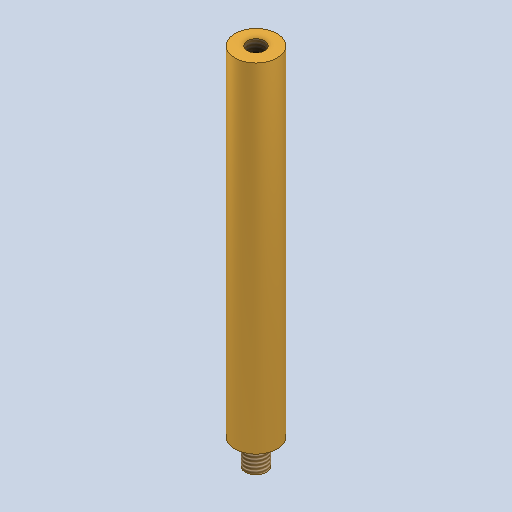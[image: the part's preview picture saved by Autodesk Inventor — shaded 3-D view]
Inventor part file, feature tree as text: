
AUTODESK INVENTOR PART (.ipt)
format: ipt  version: 2023 (Build 270158000, 158)  size: 111,104 bytes
history: native  units: mm
features: sketch x3, extrude x2, other x1, thread x1, hole x1
ambient origin geometry x8: Origin, YZ Plane, XZ Plane, XY Plane, X Axis, Y Axis, Z Axis, Center Point
bodies: Body1 (feature_tree)
feature tree (8):
  other  "Sólido1"
  extrude  "Extrusão1"  Depth=80.0mm TaperAngle=0.0deg
  extrude  "Extrusão3"  Depth=6.0mm TaperAngle=0.0deg
  thread  "Rosca2"  [1 undecoded]
  hole  "Hole1"  [1 undecoded]
  sketch  "Esboço1"  dims[d0=10.0mm d2=80.0mm d3=0.0mm]
  sketch  "Esboço3"  dims[d9=5.0mm d10=6.0mm d11=0.0mm d12=15.0mm d13=0.0mm]
  sketch  "Sketch4"  dims[d14=4.134mm d15=10.0mm d16=4.0mm d17=2.0mm d18=90.0deg d19=14.2mm d20=20.594885mm]
note: 2 required parameter values undecoded (feature->parameter linkage not recoverable at this tier; creation-order binding heuristic only, values carry confidence <= 0.55)
